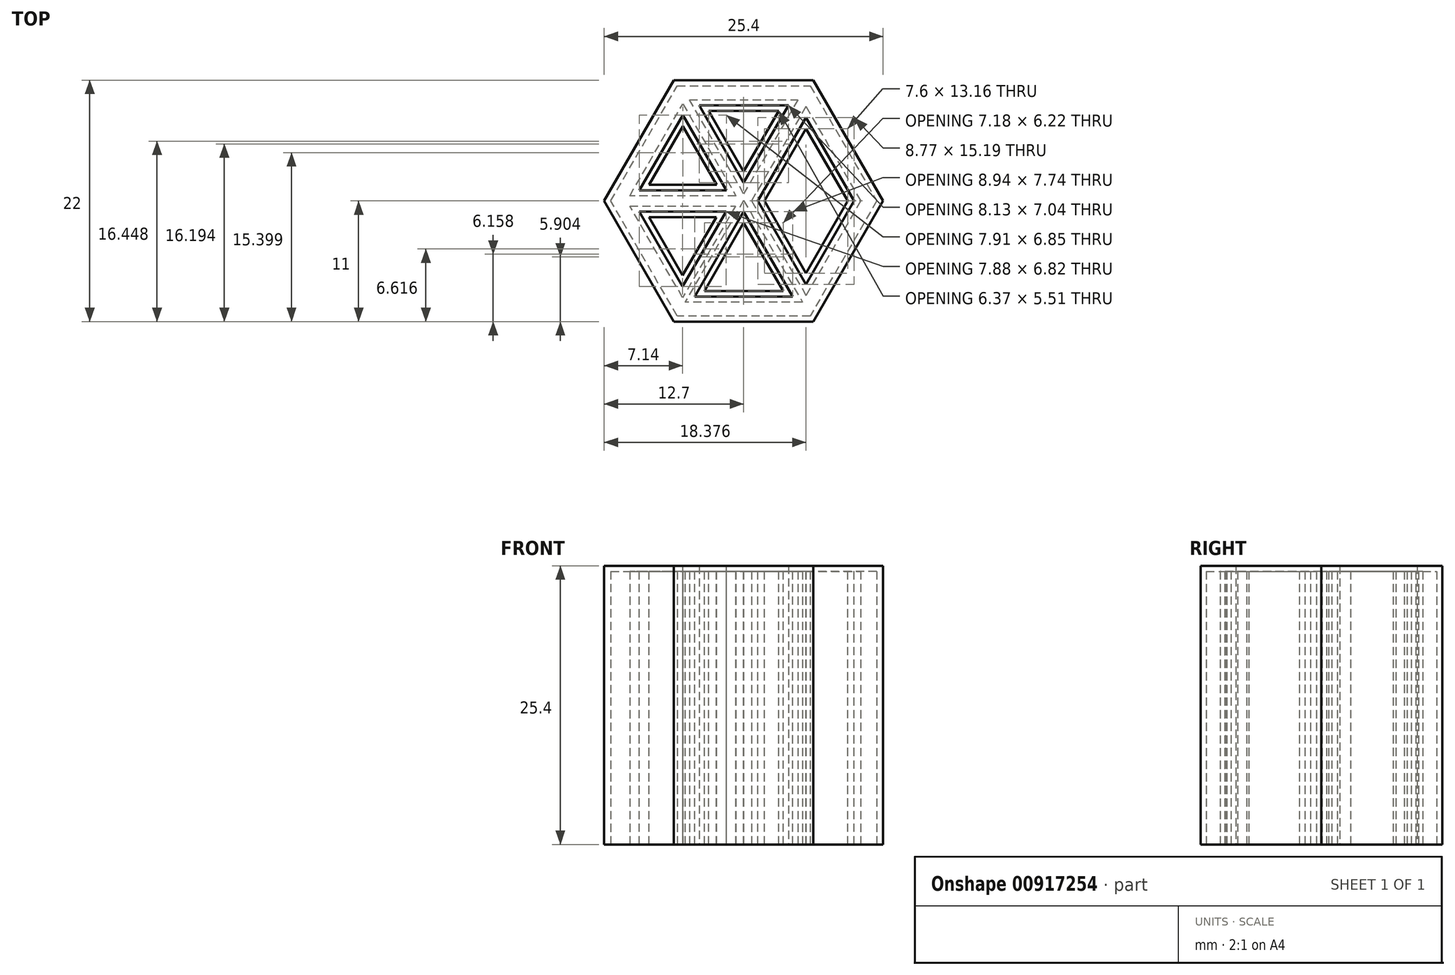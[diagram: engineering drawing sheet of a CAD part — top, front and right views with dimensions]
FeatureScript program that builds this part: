
annotation { "Feature Type Name" : "Feature", "Feature Type Description" : "" }
export const myFeature = defineFeature(function(context is Context, id is Id, definition is map)
    precondition{}
    {
        {
            var Q0;
            Q0=qCreatedBy(makeId("Top.planeOp"),FACE);
            var sketch = newSketch(context, id + "F0", { "sketchPlane" : qUnion([Q0])});
            skLineSegment(sketch, "E0.bottom", {"start": v(-12.7, 12.7) * mm, "end": v(12.7, 12.7) * mm, "construction": true});
            skLineSegment(sketch, "E0.top", {"start": v(-12.7, -12.7) * mm, "end": v(12.7, -12.7) * mm, "construction": true});
            skLineSegment(sketch, "E0.left", {"start": v(-12.7, 12.7) * mm, "end": v(-12.7, -12.7) * mm, "construction": true});
            skLineSegment(sketch, "E0.right", {"start": v(12.7, 12.7) * mm, "end": v(12.7, -12.7) * mm, "construction": true});
            skPoint(sketch, "E0.middle", {"position": v(0, 0) * mm});
            skLineSegment(sketch, "E1", {"start": v(12.7, 12.7) * mm, "end": v(0, 0) * mm, "construction": true});
            skLineSegment(sketch, "E2", {"start": v(0, 0) * mm, "end": v(-12.7, -12.7) * mm, "construction": true});
            skLineSegment(sketch, "E3", {"start": v(-12.7, 12.7) * mm, "end": v(12.7, -12.7) * mm, "construction": true});
            skLineSegment(sketch, "E4", {"start": v(-12.7, 0) * mm, "end": v(0, 0) * mm, "construction": true});
            skLineSegment(sketch, "E5", {"start": v(0, 0) * mm, "end": v(12.7, 0) * mm, "construction": true});
            skLineSegment(sketch, "E6", {"start": v(12.7, 0) * mm, "end": v(0, 12.7) * mm, "construction": true});
            skLineSegment(sketch, "E7", {"start": v(0, 12.7) * mm, "end": v(-12.7, 0) * mm, "construction": true});
            skLineSegment(sketch, "E8", {"start": v(0, -12.7) * mm, "end": v(-12.7, 0) * mm, "construction": true});
            skLineSegment(sketch, "E9", {"start": v(0, -12.7) * mm, "end": v(12.7, 0) * mm, "construction": true});
            skLineSegment(sketch, "E10", {"start": v(0, 12.7) * mm, "end": v(0, -12.7) * mm, "construction": true});
            skCircle(sketch, "E11.cCircle", {"center": v(0, 0) * mm, "radius": 11 * mm, "construction": true});
            skLineSegment(sketch, "E11.0", {"start": v(-6.35, 11) * mm, "end": v(6.35, 11) * mm, "construction": true});
            skLineSegment(sketch, "E11.1", {"start": v(6.35, 11) * mm, "end": v(12.7, 0) * mm, "construction": true});
            skLineSegment(sketch, "E11.2", {"start": v(12.7, 0) * mm, "end": v(6.35, -11) * mm, "construction": true});
            skLineSegment(sketch, "E11.3", {"start": v(6.35, -11) * mm, "end": v(-6.35, -11) * mm, "construction": true});
            skLineSegment(sketch, "E11.4", {"start": v(-6.35, -11) * mm, "end": v(-12.7, 0) * mm, "construction": true});
            skLineSegment(sketch, "E11.5", {"start": v(-12.7, 0) * mm, "end": v(-6.35, 11) * mm, "construction": true});
            skPoint(sketch, "E11.0.midPoint", {"position": v(0, 11) * mm});
            skLineSegment(sketch, "E12", {"start": v(0, 11) * mm, "end": v(0, -11) * mm, "construction": true});
            skCircle(sketch, "E13.cCircle", {"center": v(0, 0) * mm, "radius": 8.71 * mm, "construction": true});
            skLineSegment(sketch, "E13.0", {"start": v(-10.06, 0) * mm, "end": v(-5.03, 8.71) * mm, "construction": true});
            skLineSegment(sketch, "E13.1", {"start": v(-5.03, 8.71) * mm, "end": v(5.03, 8.71) * mm, "construction": true});
            skLineSegment(sketch, "E13.2", {"start": v(5.03, 8.71) * mm, "end": v(10.06, 0) * mm, "construction": true});
            skLineSegment(sketch, "E13.3", {"start": v(10.06, 0) * mm, "end": v(5.03, -8.71) * mm, "construction": true});
            skLineSegment(sketch, "E13.4", {"start": v(5.03, -8.71) * mm, "end": v(-5.03, -8.71) * mm, "construction": true});
            skLineSegment(sketch, "E13.5", {"start": v(-5.03, -8.71) * mm, "end": v(-10.06, 0) * mm, "construction": true});
            skPoint(sketch, "E13.0.midPoint", {"position": v(-7.55, 4.36) * mm});
            skSolve(sketch);
        }
        {
            var Q0;
            Q0=qCreatedBy(makeId("Top.planeOp"),FACE);
            var sketch = newSketch(context, id + "F1", { "sketchPlane" : qUnion([Q0])});
            skCircle(sketch, "E14.cCircle", {"center": v(0, 0) * mm, "radius": 11 * mm, "construction": true});
            skLineSegment(sketch, "E14.0", {"start": v(-12.7, 0) * mm, "end": v(-6.35, 11) * mm});
            skLineSegment(sketch, "E14.1", {"start": v(-6.35, 11) * mm, "end": v(6.35, 11) * mm});
            skLineSegment(sketch, "E14.2", {"start": v(6.35, 11) * mm, "end": v(12.7, 0) * mm});
            skLineSegment(sketch, "E14.3", {"start": v(12.7, 0) * mm, "end": v(6.35, -11) * mm});
            skLineSegment(sketch, "E14.4", {"start": v(6.35, -11) * mm, "end": v(-6.35, -11) * mm});
            skLineSegment(sketch, "E14.5", {"start": v(-6.35, -11) * mm, "end": v(-12.7, 0) * mm});
            skPoint(sketch, "E14.0.midPoint", {"position": v(-9.53, 5.5) * mm});
            skPoint(sketch, "E15.0.midPoint", {"position": v(-7.55, 4.36) * mm});
            skLineSegment(sketch, "E16", {"start": v(-5.03, 8.71) * mm, "end": v(5.03, -8.71) * mm, "construction": true});
            skLineSegment(sketch, "E17", {"start": v(5.03, 8.71) * mm, "end": v(-5.03, -8.71) * mm, "construction": true});
            skLineSegment(sketch, "E18", {"start": v(-10.06, 0) * mm, "end": v(10.06, 0) * mm, "construction": true});
            skLineSegment(sketch, "E19", {"start": v(5.68, 7.6) * mm, "end": v(1.3, 0) * mm});
            skLineSegment(sketch, "E20", {"start": v(1.3, 0) * mm, "end": v(5.68, -7.6) * mm});
            skLineSegment(sketch, "E21", {"start": v(4.06, 8.71) * mm, "end": v(0, 1.68) * mm});
            skLineSegment(sketch, "E22", {"start": v(0, 1.68) * mm, "end": v(-4.06, 8.71) * mm});
            skLineSegment(sketch, "E23", {"start": v(-5.54, 7.83) * mm, "end": v(-1.59, 0.97) * mm});
            skLineSegment(sketch, "E24", {"start": v(-1.59, 0.97) * mm, "end": v(-9.5, 0.97) * mm});
            skLineSegment(sketch, "E25", {"start": v(-9.5, -0.97) * mm, "end": v(-1.62, -0.97) * mm});
            skLineSegment(sketch, "E26", {"start": v(-1.62, -0.97) * mm, "end": v(-5.56, -7.8) * mm});
            skLineSegment(sketch, "E27", {"start": v(0, -0.97) * mm, "end": v(-4.47, -8.71) * mm});
            skLineSegment(sketch, "E28", {"start": v(-4.47, -8.71) * mm, "end": v(0, -0.97) * mm});
            skLineSegment(sketch, "E29", {"start": v(0, -0.97) * mm, "end": v(4.47, -8.71) * mm});
            skLineSegment(sketch, "E30", {"start": v(5.68, 7.6) * mm, "end": v(10.06, 0) * mm});
            skLineSegment(sketch, "E31", {"start": v(10.06, 0) * mm, "end": v(5.68, -7.6) * mm});
            skLineSegment(sketch, "E32", {"start": v(4.47, -8.71) * mm, "end": v(-4.47, -8.71) * mm});
            skLineSegment(sketch, "E33", {"start": v(-5.56, -7.8) * mm, "end": v(-9.5, -0.97) * mm});
            skLineSegment(sketch, "E34", {"start": v(-9.5, 0.97) * mm, "end": v(-5.54, 7.83) * mm});
            skLineSegment(sketch, "E35", {"start": v(-4.06, 8.71) * mm, "end": v(4.06, 8.71) * mm});
            skSolve(sketch);
        }
        {
            var Q0;
            Q0=qCreatedBy(makeId("Top.planeOp"),FACE);
            cPlane(context, id + "F2", {"entities" : qUnion([Q0]), "cplaneType" : CPlaneType.OFFSET, "offset" : 25.4 * mm, "width" : 152.4 * mm, "height" : 152.4 * mm});
        }
        {
            var Q0;
            Q0=qCreatedBy(id+"F2.planeOp",FACE);
            var sketch = newSketch(context, id + "F3", { "sketchPlane" : qUnion([Q0])});
            skCircle(sketch, "E36.cCircle", {"center": v(0, 0) * mm, "radius": 11 * mm, "construction": true});
            skLineSegment(sketch, "E36.0", {"start": v(-12.7, 0) * mm, "end": v(-6.35, 11) * mm});
            skLineSegment(sketch, "E36.1", {"start": v(-6.35, 11) * mm, "end": v(6.35, 11) * mm});
            skLineSegment(sketch, "E36.2", {"start": v(6.35, 11) * mm, "end": v(12.7, 0) * mm});
            skLineSegment(sketch, "E36.3", {"start": v(12.7, 0) * mm, "end": v(6.35, -11) * mm});
            skLineSegment(sketch, "E36.4", {"start": v(6.35, -11) * mm, "end": v(-6.35, -11) * mm});
            skLineSegment(sketch, "E36.5", {"start": v(-6.35, -11) * mm, "end": v(-12.7, 0) * mm});
            skPoint(sketch, "E36.0.midPoint", {"position": v(-9.53, 5.5) * mm});
            skLineSegment(sketch, "E37", {"start": v(5.68, 7.6) * mm, "end": v(1.3, 0) * mm});
            skLineSegment(sketch, "E38", {"start": v(1.3, 0) * mm, "end": v(5.68, -7.6) * mm});
            skLineSegment(sketch, "E39", {"start": v(5.68, -7.6) * mm, "end": v(10.06, 0) * mm});
            skLineSegment(sketch, "E40", {"start": v(10.06, 0) * mm, "end": v(5.68, 7.6) * mm});
            skLineSegment(sketch, "E41", {"start": v(4.06, 8.71) * mm, "end": v(0, 1.68) * mm});
            skLineSegment(sketch, "E42", {"start": v(0, 1.68) * mm, "end": v(-4.06, 8.71) * mm});
            skLineSegment(sketch, "E43", {"start": v(-4.06, 8.71) * mm, "end": v(4.06, 8.71) * mm});
            skLineSegment(sketch, "E44", {"start": v(-5.54, 7.83) * mm, "end": v(-9.5, 0.97) * mm});
            skLineSegment(sketch, "E45", {"start": v(-9.5, 0.97) * mm, "end": v(-1.59, 0.97) * mm});
            skLineSegment(sketch, "E46", {"start": v(-1.59, 0.97) * mm, "end": v(-5.54, 7.83) * mm});
            skLineSegment(sketch, "E47", {"start": v(-9.5, -0.97) * mm, "end": v(-1.62, -0.97) * mm});
            skLineSegment(sketch, "E48", {"start": v(-1.62, -0.97) * mm, "end": v(-5.56, -7.8) * mm});
            skLineSegment(sketch, "E49", {"start": v(-5.56, -7.8) * mm, "end": v(-9.5, -0.97) * mm});
            skLineSegment(sketch, "E50", {"start": v(0, -0.97) * mm, "end": v(-4.47, -8.71) * mm});
            skLineSegment(sketch, "E51", {"start": v(-4.47, -8.71) * mm, "end": v(4.47, -8.71) * mm});
            skLineSegment(sketch, "E52", {"start": v(4.47, -8.71) * mm, "end": v(0, -0.97) * mm});
            skSolve(sketch);
        }
        {
            var Q0;
            Q0=makeQuery(id+"F1.imprint","IMPRINT",FACE,{"disambiguationData":[TD([[makeQuery(id+"F1.imprint","IMPRINT",EDGE,{"derivedFrom":sQuery(id+"F1.wireOp",EDGE,"E14.0")}),-1.0]])]});
            extrude(context, id + "F4", {"entities" : qUnion([Q0]), "depth" : 25.4 * mm, "offsetDistance" : 25.4 * mm});
        }
        {
            var Q0;
            Q0=makeQuery(id+"F3.imprint","IMPRINT",FACE,{"disambiguationData":[TD([[makeQuery(id+"F3.imprint","IMPRINT",EDGE,{"derivedFrom":sQuery(id+"F3.wireOp",EDGE,"E37")}),1.0]])]});
            var Q1;
            Q1=makeQuery(id+"F3.imprint","IMPRINT",FACE,{"disambiguationData":[TD([[makeQuery(id+"F3.imprint","IMPRINT",EDGE,{"derivedFrom":sQuery(id+"F3.wireOp",EDGE,"E41")}),-1.0]])]});
            var Q2;
            Q2=makeQuery(id+"F3.imprint","IMPRINT",FACE,{"disambiguationData":[TD([[makeQuery(id+"F3.imprint","IMPRINT",EDGE,{"derivedFrom":sQuery(id+"F3.wireOp",EDGE,"E44")}),1.0]])]});
            var Q3;
            Q3=makeQuery(id+"F3.imprint","IMPRINT",FACE,{"disambiguationData":[TD([[makeQuery(id+"F3.imprint","IMPRINT",EDGE,{"derivedFrom":sQuery(id+"F3.wireOp",EDGE,"E47")}),-1.0]])]});
            var Q4;
            Q4=makeQuery(id+"F3.imprint","IMPRINT",FACE,{"disambiguationData":[TD([[makeQuery(id+"F3.imprint","IMPRINT",EDGE,{"derivedFrom":sQuery(id+"F3.wireOp",EDGE,"E50")}),1.0]])]});
            extrude(context, id + "F5", {"entities" : qUnion([Q0, Q1, Q2, Q3, Q4]), "oppositeDirection" : true, "depth" : 25.4 * mm, "offsetDistance" : 25.4 * mm});
        }
        {
            var Q0;
            Q0=makeQuery(id+"F5.opExtrude","CAP_FACE",FACE,{"disambiguationData":[OSD([sQuery(id+"F3.wireOp",EDGE,"E37"),sQuery(id+"F3.wireOp",EDGE,"E38"),sQuery(id+"F3.wireOp",EDGE,"E39"),sQuery(id+"F3.wireOp",EDGE,"E40")])],"isStart":false});
            var Q1;
            Q1=makeQuery(id+"F5.opExtrude","CAP_FACE",FACE,{"disambiguationData":[OSD([sQuery(id+"F3.wireOp",EDGE,"E50"),sQuery(id+"F3.wireOp",EDGE,"E51"),sQuery(id+"F3.wireOp",EDGE,"E52")])],"isStart":false});
            var Q2;
            Q2=makeQuery(id+"F5.opExtrude","CAP_FACE",FACE,{"disambiguationData":[OSD([sQuery(id+"F3.wireOp",EDGE,"E47"),sQuery(id+"F3.wireOp",EDGE,"E48"),sQuery(id+"F3.wireOp",EDGE,"E49")])],"isStart":false});
            var Q3;
            Q3=makeQuery(id+"F5.opExtrude","CAP_FACE",FACE,{"disambiguationData":[OSD([sQuery(id+"F3.wireOp",EDGE,"E44"),sQuery(id+"F3.wireOp",EDGE,"E45"),sQuery(id+"F3.wireOp",EDGE,"E46")])],"isStart":false});
            var Q4;
            Q4=makeQuery(id+"F5.opExtrude","CAP_FACE",FACE,{"disambiguationData":[OSD([sQuery(id+"F3.wireOp",EDGE,"E41"),sQuery(id+"F3.wireOp",EDGE,"E42"),sQuery(id+"F3.wireOp",EDGE,"E43")])],"isStart":false});
            var Q5;
            Q5=makeQuery(id+"F5.opExtrude","CAP_FACE",FACE,{"disambiguationData":[OSD([sQuery(id+"F3.wireOp",EDGE,"E44"),sQuery(id+"F3.wireOp",EDGE,"E45"),sQuery(id+"F3.wireOp",EDGE,"E46")])],"isStart":true});
            var Q6;
            Q6=makeQuery(id+"F5.opExtrude","CAP_FACE",FACE,{"disambiguationData":[OSD([sQuery(id+"F3.wireOp",EDGE,"E41"),sQuery(id+"F3.wireOp",EDGE,"E42"),sQuery(id+"F3.wireOp",EDGE,"E43")])],"isStart":true});
            var Q7;
            Q7=makeQuery(id+"F5.opExtrude","CAP_FACE",FACE,{"disambiguationData":[OSD([sQuery(id+"F3.wireOp",EDGE,"E37"),sQuery(id+"F3.wireOp",EDGE,"E38"),sQuery(id+"F3.wireOp",EDGE,"E39"),sQuery(id+"F3.wireOp",EDGE,"E40")])],"isStart":true});
            var Q8;
            Q8=makeQuery(id+"F5.opExtrude","CAP_FACE",FACE,{"disambiguationData":[OSD([sQuery(id+"F3.wireOp",EDGE,"E50"),sQuery(id+"F3.wireOp",EDGE,"E51"),sQuery(id+"F3.wireOp",EDGE,"E52")])],"isStart":true});
            var Q9;
            Q9=makeQuery(id+"F5.opExtrude","CAP_FACE",FACE,{"disambiguationData":[OSD([sQuery(id+"F3.wireOp",EDGE,"E47"),sQuery(id+"F3.wireOp",EDGE,"E48"),sQuery(id+"F3.wireOp",EDGE,"E49")])],"isStart":true});
            shell(context, id + "F6", {"entities" : qUnion([Q0, Q1, Q2, Q3, Q4, Q5, Q6, Q7, Q8, Q9]), "thickness" : 0.5 * mm});
        }
        {
            var Q0;
            Q0=makeQuery(id+"F4.opExtrude","CAP_FACE",FACE,{"disambiguationData":[OSD([sQuery(id+"F1.wireOp",EDGE,"E14.0"),sQuery(id+"F1.wireOp",EDGE,"E14.1"),sQuery(id+"F1.wireOp",EDGE,"E14.2"),sQuery(id+"F1.wireOp",EDGE,"E14.3"),sQuery(id+"F1.wireOp",EDGE,"E14.4"),sQuery(id+"F1.wireOp",EDGE,"E14.5"),sQuery(id+"F1.wireOp",EDGE,"E19"),sQuery(id+"F1.wireOp",EDGE,"E20"),sQuery(id+"F1.wireOp",EDGE,"E21"),sQuery(id+"F1.wireOp",EDGE,"E22"),sQuery(id+"F1.wireOp",EDGE,"E23"),sQuery(id+"F1.wireOp",EDGE,"E24"),sQuery(id+"F1.wireOp",EDGE,"E25"),sQuery(id+"F1.wireOp",EDGE,"E26"),sQuery(id+"F1.wireOp",EDGE,"E28"),sQuery(id+"F1.wireOp",EDGE,"E29"),sQuery(id+"F1.wireOp",EDGE,"E30"),sQuery(id+"F1.wireOp",EDGE,"E31"),sQuery(id+"F1.wireOp",EDGE,"E32"),sQuery(id+"F1.wireOp",EDGE,"E33"),sQuery(id+"F1.wireOp",EDGE,"E34"),sQuery(id+"F1.wireOp",EDGE,"E35")])],"isStart":true});
            shell(context, id + "F7", {"entities" : qUnion([Q0]), "thickness" : 0.5 * mm});
        }
    });
